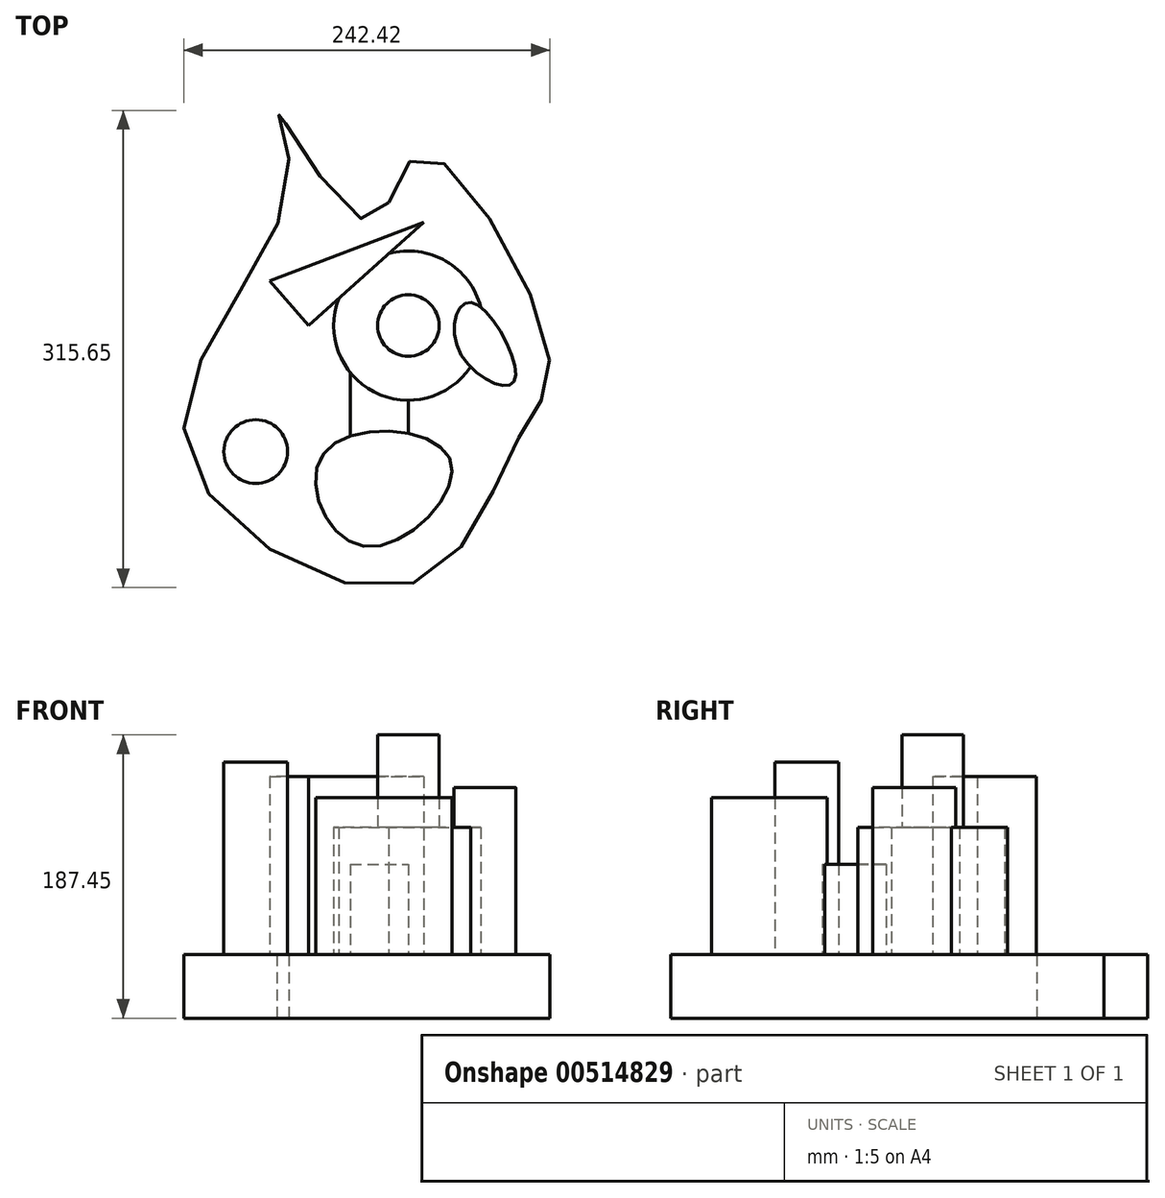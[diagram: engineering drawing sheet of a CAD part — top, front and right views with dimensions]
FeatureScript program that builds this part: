
annotation { "Feature Type Name" : "Feature", "Feature Type Description" : "" }
export const myFeature = defineFeature(function(context is Context, id is Id, definition is map)
    precondition{}
    {
        {
            var Q0;
            Q0=qCreatedBy(makeId("Top.planeOp"),FACE);
            var sketch = newSketch(context, id + "F0", { "sketchPlane" : qUnion([Q0])});
            skFitSpline(sketch, "E0", {"points": [v(73.02, -74.1) * mm, v(0, -171.31) * mm, v(-147.67, -77.44) * mm, v(-79.38, 92.33) * mm, v(-85.98, 141.7) * mm, v(-25.4, 69.27) * mm, v(7.17, 113.1) * mm, v(92.59, -15.88) * mm, v(73.02, -74.1) * mm]});
            skSolve(sketch);
        }
        {
            var Q0;
            Q0 = qSketchRegion(id + "F0", true);
            extrude(context, id + "F1", {"entities" : qUnion([Q0]), "oppositeDirection" : true, "depth" : 42.16 * mm, "offsetDistance" : 25.4 * mm});
        }
        {
            var Q0;
            Q0=qCreatedBy(makeId("Top.planeOp"),FACE);
            var sketch = newSketch(context, id + "F2", { "sketchPlane" : qUnion([Q0])});
            skLineSegment(sketch, "E1.bottom", {"start": v(-38.52, -127.34) * mm, "end": v(0, -127.34) * mm});
            skLineSegment(sketch, "E1.top", {"start": v(-38.52, 0) * mm, "end": v(0, 0) * mm});
            skLineSegment(sketch, "E1.left", {"start": v(-38.52, -127.34) * mm, "end": v(-38.52, 0) * mm});
            skLineSegment(sketch, "E1.right", {"start": v(0, -127.34) * mm, "end": v(0, 0) * mm});
            skSolve(sketch);
        }
        {
            var Q0;
            Q0 = qSketchRegion(id + "F2", true);
            extrude(context, id + "F3", {"entities" : qUnion([Q0]), "operationType" : NewBodyOperationType.ADD, "depth" : 59.69 * mm, "offsetDistance" : 25.4 * mm});
        }
        {
            var Q0;
            Q0=qCreatedBy(makeId("Top.planeOp"),FACE);
            var sketch = newSketch(context, id + "F4", { "sketchPlane" : qUnion([Q0])});
            skFitSpline(sketch, "E2", {"points": [v(70.03, -37) * mm, v(33.23, -16.08) * mm, v(42.07, 15.2) * mm, v(70.03, -37) * mm]});
            skSolve(sketch);
        }
        {
            var Q0;
            Q0 = qSketchRegion(id + "F4", true);
            extrude(context, id + "F5", {"entities" : qUnion([Q0]), "operationType" : NewBodyOperationType.ADD, "depth" : 110.49 * mm, "offsetDistance" : 25.4 * mm});
        }
        {
            var Q0;
            Q0=qCreatedBy(makeId("Top.planeOp"),FACE);
            var sketch = newSketch(context, id + "F6", { "sketchPlane" : qUnion([Q0])});
            skCircle(sketch, "E3", {"center": v(-100.97, -83.38) * mm, "radius": 21.11 * mm});
            skSolve(sketch);
        }
        {
            var Q0;
            Q0 = qSketchRegion(id + "F6", true);
            extrude(context, id + "F7", {"entities" : qUnion([Q0]), "operationType" : NewBodyOperationType.ADD, "depth" : 127.25 * mm, "offsetDistance" : 25.4 * mm});
        }
        {
            var Q0;
            Q0=qCreatedBy(makeId("Top.planeOp"),FACE);
            var sketch = newSketch(context, id + "F8", { "sketchPlane" : qUnion([Q0])});
            skCircle(sketch, "E4", {"center": v(0, 0) * mm, "radius": 20.32 * mm});
            skSolve(sketch);
        }
        {
            var Q0;
            Q0 = qSketchRegion(id + "F8", true);
            extrude(context, id + "F9", {"entities" : qUnion([Q0]), "operationType" : NewBodyOperationType.ADD, "depth" : 145.29 * mm, "offsetDistance" : 25.4 * mm});
        }
        {
            var Q0;
            Q0=qCreatedBy(makeId("Top.planeOp"),FACE);
            var sketch = newSketch(context, id + "F10", { "sketchPlane" : qUnion([Q0])});
            skFitSpline(sketch, "E5", {"points": [v(-29.43, -146.03) * mm, v(-55.18, -83.56) * mm, v(27.82, -88.92) * mm, v(-29.43, -146.03) * mm]});
            skSolve(sketch);
        }
        {
            var Q0;
            Q0 = qSketchRegion(id + "F10", true);
            extrude(context, id + "F11", {"entities" : qUnion([Q0]), "operationType" : NewBodyOperationType.ADD, "depth" : 103.63 * mm, "offsetDistance" : 25.4 * mm});
        }
        {
            var Q0;
            Q0=qCreatedBy(makeId("Top.planeOp"),FACE);
            var sketch = newSketch(context, id + "F12", { "sketchPlane" : qUnion([Q0])});
            skLineSegment(sketch, "E6", {"start": v(-91.82, 29.49) * mm, "end": v(10.14, 68.44) * mm});
            skLineSegment(sketch, "E7", {"start": v(10.14, 68.44) * mm, "end": v(-65.87, 0) * mm});
            skLineSegment(sketch, "E8", {"start": v(-65.87, 0) * mm, "end": v(-91.82, 29.49) * mm});
            skSolve(sketch);
        }
        {
            var Q0;
            Q0 = qSketchRegion(id + "F12", true);
            extrude(context, id + "F13", {"entities" : qUnion([Q0]), "operationType" : NewBodyOperationType.ADD, "depth" : 117.6 * mm, "offsetDistance" : 25.4 * mm});
        }
        {
            var Q0;
            Q0=makeQuery(id+"F1.opExtrude","CAP_FACE",FACE,{"disambiguationData":[OSD([sQuery(id+"F0.wireOp",EDGE,"E0")])],"isStart":true});
            var sketch = newSketch(context, id + "F14", { "sketchPlane" : qUnion([Q0])});
            skCircle(sketch, "E9", {"center": v(0, 0) * mm, "radius": 49.41 * mm});
            skSolve(sketch);
        }
        {
            var Q0;
            Q0 = qSketchRegion(id + "F14", true);
            extrude(context, id + "F15", {"entities" : qUnion([Q0]), "operationType" : NewBodyOperationType.ADD, "depth" : 84.07 * mm, "offsetDistance" : 25.4 * mm});
        }
    });
